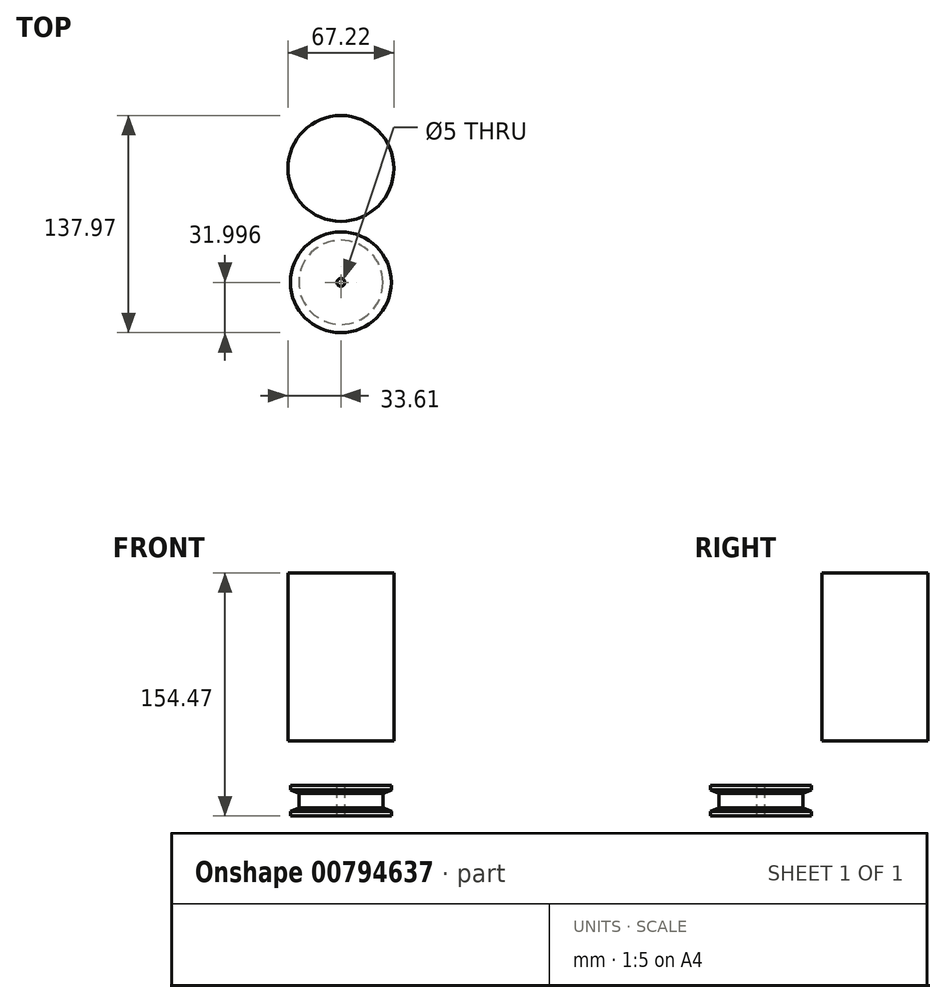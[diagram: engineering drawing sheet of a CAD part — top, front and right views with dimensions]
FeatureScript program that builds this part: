
annotation { "Feature Type Name" : "Feature", "Feature Type Description" : "" }
export const myFeature = defineFeature(function(context is Context, id is Id, definition is map)
    precondition{}
    {
        {
            var Q0;
            Q0=qCreatedBy(makeId("Top.planeOp"),FACE);
            var sketch = newSketch(context, id + "F0", { "sketchPlane" : qUnion([Q0])});
            skCircle(sketch, "E0", {"center": v(0, 0) * mm, "radius": 33.61 * mm});
            skSolve(sketch);
        }
        {
            var Q0;
            Q0=makeQuery(id+"F0.imprint","IMPRINT",FACE,{"disambiguationData":[TD([[makeQuery(id+"F0.imprint","IMPRINT",EDGE,{"derivedFrom":sQuery(id+"F0.wireOp",EDGE,"E0")}),1.0]])]});
            extrude(context, id + "F1", {"entities" : qUnion([Q0]), "depth" : 106.7 * mm, "offsetDistance" : 25 * mm});
        }
        {
            var Q0;
            Q0=qCreatedBy(makeId("Right.planeOp"),FACE);
            var sketch = newSketch(context, id + "F2", { "sketchPlane" : qUnion([Q0])});
            skLineSegment(sketch, "E1.bottom", {"start": v(-104.36, -28.28) * mm, "end": v(-72.36, -28.28) * mm});
            skLineSegment(sketch, "E1.top", {"start": v(-104.36, -47.77) * mm, "end": v(-72.36, -47.77) * mm});
            skLineSegment(sketch, "E1.right", {"start": v(-72.36, -28.28) * mm, "end": v(-72.36, -47.77) * mm});
            skLineSegment(sketch, "E2", {"start": v(-104.36, -28.28) * mm, "end": v(-104.36, -31.28) * mm});
            skLineSegment(sketch, "E3", {"start": v(-104.36, -31.28) * mm, "end": v(-99.08, -33.52) * mm});
            skLineSegment(sketch, "E4", {"start": v(-99.08, -33.52) * mm, "end": v(-99.08, -42.52) * mm});
            skLineSegment(sketch, "E5", {"start": v(-99.08, -42.52) * mm, "end": v(-104.36, -44.77) * mm});
            skLineSegment(sketch, "E6", {"start": v(-104.36, -44.77) * mm, "end": v(-104.36, -47.77) * mm});
            skSolve(sketch);
        }
        {
            var Q0;
            Q0=makeQuery(id+"F2.imprint","IMPRINT",FACE,{"disambiguationData":[TD([[makeQuery(id+"F2.imprint","IMPRINT",EDGE,{"derivedFrom":sQuery(id+"F2.wireOp",EDGE,"E1.bottom")}),-1.0]])]});
            var Q1;
            Q1=sQuery(id+"F2.wireOp",EDGE,"E1.right");
            revolve(context, id + "F3", {"surfaceOperationType" : NewSurfaceOperationType.NEW, "entities" : qUnion([Q0]), "axis" : qUnion([Q1]), "revolveType" : RevolveType.FULL});
        }
        {
            var Q0;
            Q0=makeQuery(id+"F3.opRevolve","SWEPT_FACE",FACE,{"disambiguationData":[OSD([sQuery(id+"F2.wireOp",EDGE,"E1.bottom")])]});
            var sketch = newSketch(context, id + "F4", { "sketchPlane" : qUnion([Q0])});
            skCircle(sketch, "E7", {"center": v(0, -72.36) * mm, "radius": 2.5 * mm});
            skSolve(sketch);
        }
        {
            var Q0;
            Q0=makeQuery(id+"F4.imprint","IMPRINT",FACE,{"disambiguationData":[TD([[makeQuery(id+"F4.imprint","IMPRINT",EDGE,{"derivedFrom":sQuery(id+"F4.wireOp",EDGE,"E7")}),1.0]])]});
            extrude(context, id + "F5", {"entities" : qUnion([Q0]), "operationType" : NewBodyOperationType.REMOVE, "oppositeDirection" : true, "depth" : 27.2 * mm, "offsetDistance" : 25 * mm});
        }
    });
